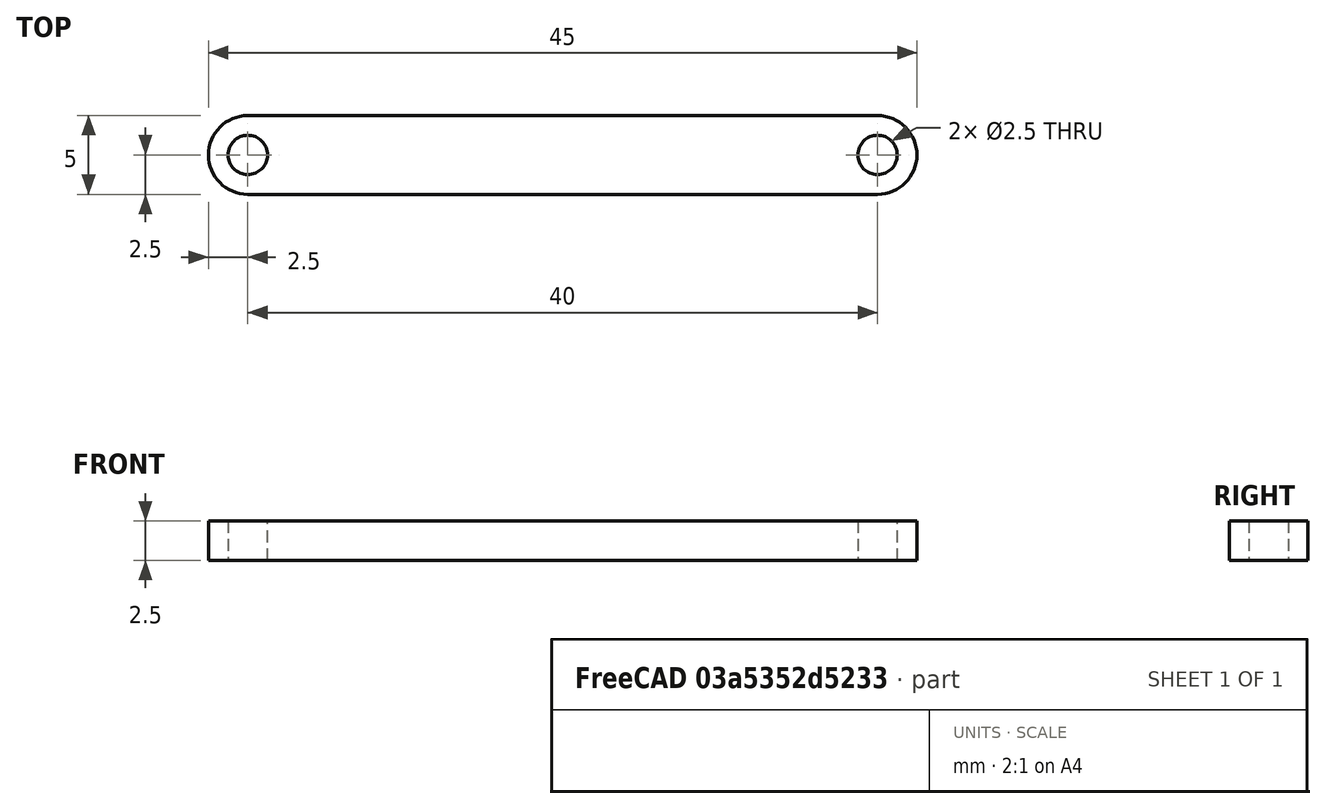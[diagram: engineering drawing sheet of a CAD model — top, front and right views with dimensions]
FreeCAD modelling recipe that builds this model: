
FCSTD DOCUMENT  (FreeCAD 0.20R29410 (Git))
Label: Eslabon1
License: All rights reserved
LicenseURL: http://en.wikipedia.org/wiki/All_rights_reserved
objects: Sketcher::SketchObject×1, Part::Extrusion×1
note: 2 computed .brp shape members not serialized (recipe doc carries the construction recipe); baked Part::Feature solids carry a one-line shape summary decoded from their .brp

FEATURE [Sketcher::SketchObject] Sketch  label="Eslabon 40x2.5mm, hoyo r1mm"
  FullyConstrained = true
  sketch-geometry (6):
    g0: LineSegment StartX=2e-16 StartY=2.5 StartZ=0 EndX=40 EndY=2.5 EndZ=0
    g1: LineSegment StartX=0 StartY=-2.5 StartZ=0 EndX=40 EndY=-2.5 EndZ=0
    g2: ArcOfCircle CenterX=0 CenterY=0 CenterZ=0 NormalX=0 NormalY=0 NormalZ=1 AngleXU=0 Radius=2.5 StartAngle=1.5708 EndAngle=4.71239
    g3: ArcOfCircle CenterX=40 CenterY=1e-16 CenterZ=0 NormalX=0 NormalY=0 NormalZ=1 AngleXU=0 Radius=2.5 StartAngle=4.71239 EndAngle=7.85398
    g4: Circle CenterX=0 CenterY=0 CenterZ=0 NormalX=0 NormalY=0 NormalZ=1 AngleXU=0 Radius=1.25
    g5: Circle CenterX=40 CenterY=1e-16 CenterZ=0 NormalX=0 NormalY=0 NormalZ=1 AngleXU=0 Radius=1.25
  constraints (18):
    c: PointOnObject(g0,g-2)
    c: PointOnObject(g1,g-2)
    c: Horizontal(g0)
    c: Horizontal(g1)
    c: Equal(g0,g1)
    c: Distance(g0) = 40
    c: DistanceY(g1,g0) = 5
    c: DistanceY(g-1,g0) = 2.5
    c: Coincident(g2,g-1)
    c: Coincident(g2,g0)
    c: PointOnObject(g2,g-2)
    c: Coincident(g3,g0)
    c: Coincident(g3,g1)
    c: Radius(g3) = 2.5
    c: Coincident(g4,g2)
    c: Coincident(g5,g3)
    c: Equal(g4,g5)
    c: Radius(g4) = 1.25
FEATURE [Part::Extrusion] Extrude  label="Extrusion 2.5mm"
  Base = -> Sketch
  Dir = (0,0,1)
  DirMode = 2
  FaceMakerClass = Part::FaceMakerBullseye
  LengthFwd = 2.5
  LengthRev = 0
  Solid = true
  Symmetric = false
